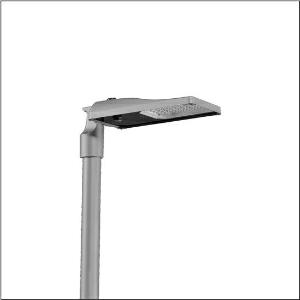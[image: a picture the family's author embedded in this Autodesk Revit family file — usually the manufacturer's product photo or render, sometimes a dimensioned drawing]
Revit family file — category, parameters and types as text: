
# Revit family: streetlight_sl_31_mini___stw1_0a_5xh6e31t08ha_3957
name_source: partatom
category: Lighting Fixtures
units: mm (PartAtom-declared; Revit-internal decimal feet)

## family parameters
Cut with Voids When Loaded = No
Host = Face
Light Source = No
Part Type = Normal
Room Calculation Point = No
Round Connector Dimension = Use Diameter
Shared = No

## types (1)
- --- (1 x LED, 9230 lm, 68.2 W, 3000K)
    Apparent Load = 68 VA
    CIE Flux Codes = 38 75 98 100 100
    Color Rendering = 70
    Color Temperature = 3000K
    Default Elevation = 1800 mm
    Description = Streetlight SL 31 mini, mast luminaire, primary light control with lens, of PMMA, primary optical cover: cover, of toughened safety glass, transparent, light distribution: STW1.0a, light emission: direct distribution, primary light characteristic: asymmetric, installation type: post-top, side-entry, LED, High Power LED, rated luminous flux: 9.230lm, luminous efficacy: 135lm/W, light colour: 730, colour temperature: 3000K, control: presetting dimming logarithmic, flexible luminous flux parameterisation, time-dependent luminous flux control, constant luminous flux control, power reduction, intelligent temperature release in ECG and LED module, overheat protection, with cable H07RN-F 2x 1.5mm², mains connection: 220..240V, AC, 50/60Hz, connection cable pre-assembled, cable length: 8,5m, start of lifetime: 68W, end of service life: 74W, reduction: 30W, luminaire housing, of diecast aluminium, powder-coated, Siteco® metallic grey (DB 702S), corrosivity category C5 high according to DIN EN ISO 12944, sealing non-destructively replaceable, multi-level sealing system, mast flange (76/60mm) included as standard, inclination: -15°..+20° (post-top) | -20°..+20° (side-entry), adjustable in 5° steps, no sealing on luminaire upper side, Smart Interface below and above, protection rating (complete): IP66, insulation class (complete): insulation class II (safety insulation), certification: CE, ENEC, ENEC+, VDE, UKCA, ZD4i, impact resistance: IK09, permissible operating ambient temperature for outdoor applications: -40..+50°C, standard-compliant lighting for roads and squares, packaging unit: 1 piece

Light Distribution: STW1.0a
    Height = 76 mm
    Lamp = 1 x LED
    Lamp Light Flux = 9230 lm
    Lamp Power = 68.2 W
    Lamp count = 1
    Length = 547 mm
    Luminous efficacy = 135 lm/W
    Manufacturer = Siteco
    ModVariant = No
    Model = 5XH6E31T08HA
    Number of Poles = 1
    OnlyDefault = Yes
    Power Factor = 1
    Product Name = Streetlight SL 31 mini | STW1.0a
    Product group = mast luminaire | pylon top
    ProductGroupID = 6100
    Protection Class = Protection class II
    Protection Degree = IP 66
    RLX_Detail_Level = 1
    RLX_Emergency_Light_Flux = 0 lm
    RLX_Emergency_Type = 0
    RLX_Emergency_Type_DB = No
    RlxData = <blob elided: 39857 chars, md5=30d2b359>
    Socket = socket
    Standby Power = 0 W
    System Light Flux = 9230 lm
    System Power = 68 W
    Type Comments = factory setting: luminous flux: 100 % | dim-lin: 254 | 692 mA
    Type Image = l_1300332.jpg
    URL = http://relux.com
    VarID = @adj_011135
    Voltage = 0 V
    Weight = 0.00 kg
    Width = 265 mm

## geometry (parser evidence)
native form markers: Blend x4, Sweep x9
no freeform markers — native parametric forms only
